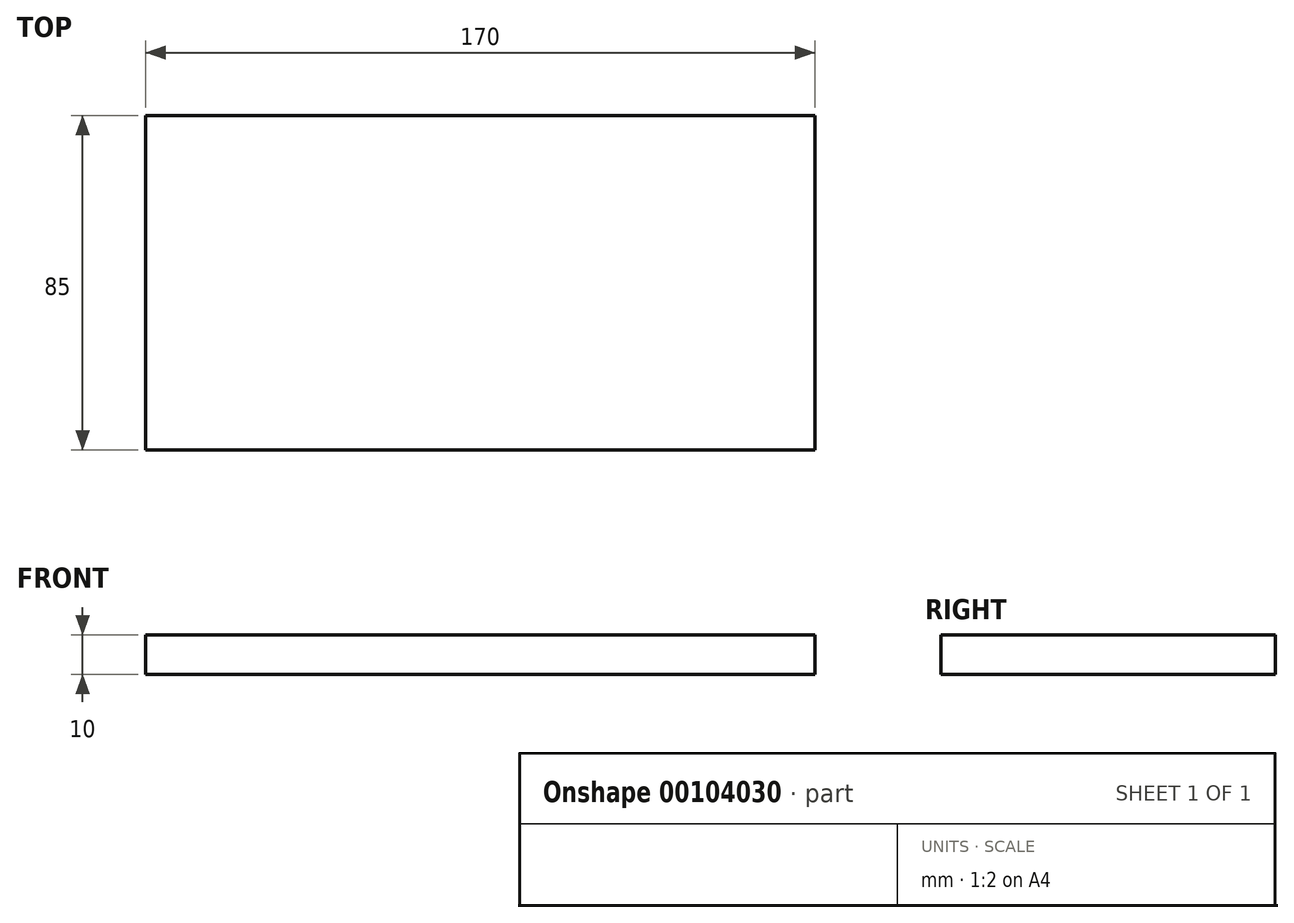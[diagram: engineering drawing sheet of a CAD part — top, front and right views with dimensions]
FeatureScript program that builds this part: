
annotation { "Feature Type Name" : "Feature", "Feature Type Description" : "" }
export const myFeature = defineFeature(function(context is Context, id is Id, definition is map)
    precondition{}
    {
        {
            var Q0;
            Q0=qCreatedBy(makeId("Top.planeOp"),FACE);
            var sketch = newSketch(context, id + "F0", { "sketchPlane" : qUnion([Q0])});
            skLineSegment(sketch, "E0.bottom", {"start": v(-102.53, 47.43) * mm, "end": v(67.47, 47.43) * mm});
            skLineSegment(sketch, "E0.top", {"start": v(-102.53, -37.57) * mm, "end": v(67.47, -37.57) * mm});
            skLineSegment(sketch, "E0.left", {"start": v(-102.53, 47.43) * mm, "end": v(-102.53, -37.57) * mm});
            skLineSegment(sketch, "E0.right", {"start": v(67.47, 47.43) * mm, "end": v(67.47, -37.57) * mm});
            skSolve(sketch);
        }
        {
            var Q0;
            Q0 = qSketchRegion(id + "F0", true);
            extrude(context, id + "F1", {"entities" : qUnion([Q0]), "flatOperationType" : FlatOperationType.REMOVE, "depth" : 10 * mm, "offsetDistance" : 25 * mm, "domain" : OperationDomain.MODEL});
        }
    });
